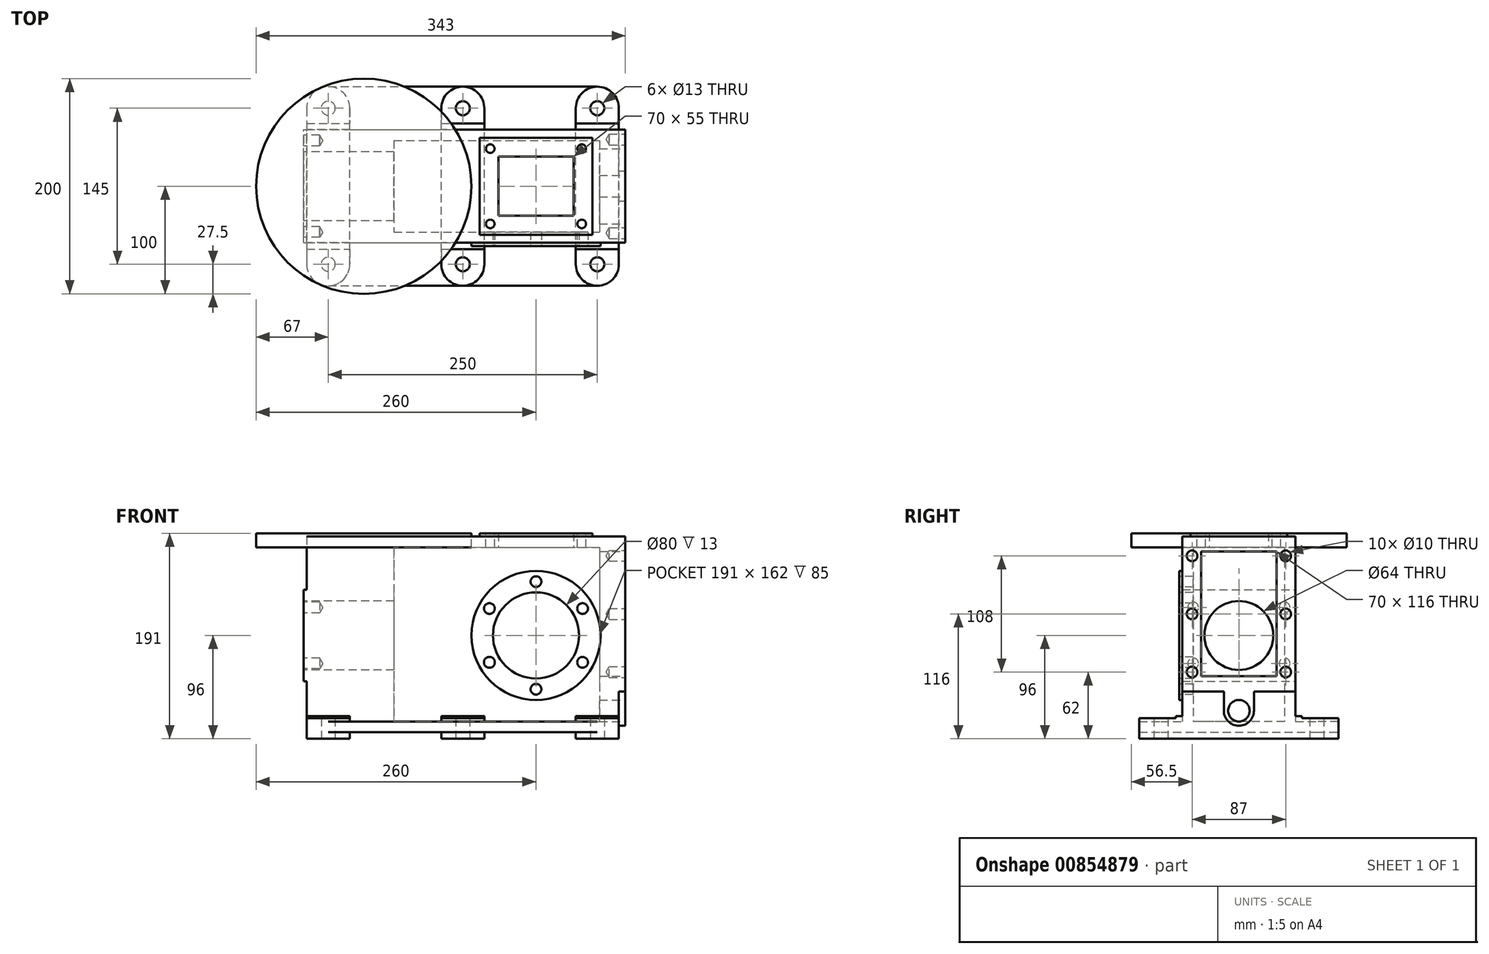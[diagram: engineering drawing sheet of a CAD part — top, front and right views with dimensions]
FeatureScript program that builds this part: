
annotation { "Feature Type Name" : "Feature", "Feature Type Description" : "" }
export const myFeature = defineFeature(function(context is Context, id is Id, definition is map)
    precondition{}
    {
        {
            var Q0;
            Q0=qCreatedBy(makeId("Top.planeOp"),FACE);
            cPlane(context, id + "F0", {"entities" : qUnion([Q0]), "cplaneType" : CPlaneType.OFFSET, "offset" : 90 * mm, "oppositeDirection" : true, "width" : 152.4 * mm, "height" : 152.4 * mm});
        }
        {
            var Q0;
            Q0=qCreatedBy(id+"F0.planeOp",FACE);
            var sketch = newSketch(context, id + "F1", { "sketchPlane" : qUnion([Q0])});
            skLineSegment(sketch, "E0", {"start": v(0, 0) * mm, "end": v(-193, 0) * mm, "construction": true});
            skLineSegment(sketch, "E1", {"start": v(-193, 72.5) * mm, "end": v(-193, -72.5) * mm, "construction": true});
            skLineSegment(sketch, "E2", {"start": v(-68, 72.5) * mm, "end": v(-68, -72.5) * mm, "construction": true});
            skLineSegment(sketch, "E3", {"start": v(57, 72.5) * mm, "end": v(57, -72.5) * mm, "construction": true});
            skLineSegment(sketch, "E4", {"start": v(-193, 72.5) * mm, "end": v(57, 72.5) * mm, "construction": true});
            skLineSegment(sketch, "E5", {"start": v(-193, -72.5) * mm, "end": v(57, -72.5) * mm, "construction": true});
            skArc(sketch, "E6", {"start": v(77, 72.5) * mm, "mid": v(57, 92.5) * mm, "end": v(37, 72.5) * mm});
            skArc(sketch, "E7", {"start": v(37, -72.5) * mm, "mid": v(57, -92.5) * mm, "end": v(77, -72.5) * mm});
            skLineSegment(sketch, "E8", {"start": v(37, 72.5) * mm, "end": v(37, -72.5) * mm});
            skLineSegment(sketch, "E9.MirrorCS", {"start": v(77, 72.5) * mm, "end": v(77, -72.5) * mm});
            skArc(sketch, "E10.1.0.0", {"start": v(-48, 72.5) * mm, "mid": v(-68, 92.5) * mm, "end": v(-88, 72.5) * mm});
            skLineSegment(sketch, "E10.1.0.1", {"start": v(-88, 72.5) * mm, "end": v(-88, -72.5) * mm});
            skLineSegment(sketch, "E10.1.0.2", {"start": v(-48, 72.5) * mm, "end": v(-48, -72.5) * mm});
            skArc(sketch, "E10.1.0.3", {"start": v(-88, -72.5) * mm, "mid": v(-68, -92.5) * mm, "end": v(-48, -72.5) * mm});
            skArc(sketch, "E10.2.0.0", {"start": v(-173, 72.5) * mm, "mid": v(-193, 92.5) * mm, "end": v(-213, 72.5) * mm});
            skLineSegment(sketch, "E10.2.0.1", {"start": v(-213, 72.5) * mm, "end": v(-213, -72.5) * mm});
            skLineSegment(sketch, "E10.2.0.2", {"start": v(-173, 72.5) * mm, "end": v(-173, -72.5) * mm});
            skArc(sketch, "E10.2.0.3", {"start": v(-213, -72.5) * mm, "mid": v(-193, -92.5) * mm, "end": v(-173, -72.5) * mm});
            skLineSegment(sketch, "E10.direction1", {"start": v(37, 72.5) * mm, "end": v(-88, 72.5) * mm, "construction": true});
            skCircle(sketch, "E11", {"center": v(57, 72.5) * mm, "radius": 6.5 * mm});
            skCircle(sketch, "E12", {"center": v(57, -72.5) * mm, "radius": 6.5 * mm});
            skCircle(sketch, "E13.1.0.0", {"center": v(-68, 72.5) * mm, "radius": 6.5 * mm});
            skCircle(sketch, "E13.1.0.1", {"center": v(-68, -72.5) * mm, "radius": 6.5 * mm});
            skCircle(sketch, "E13.2.0.0", {"center": v(-193, 72.5) * mm, "radius": 6.5 * mm});
            skCircle(sketch, "E13.2.0.1", {"center": v(-193, -72.5) * mm, "radius": 6.5 * mm});
            skLineSegment(sketch, "E13.direction1", {"start": v(57, 72.5) * mm, "end": v(-68, 72.5) * mm, "construction": true});
            skLineSegment(sketch, "E14", {"start": v(-193, 92.5) * mm, "end": v(57, 92.5) * mm});
            skLineSegment(sketch, "E15", {"start": v(-193, -92.5) * mm, "end": v(57, -92.5) * mm});
            skSolve(sketch);
        }
        {
            var Q0;
            Q0 = qSketchRegion(id + "F1", true);
            extrude(context, id + "F2", {"entities" : qUnion([Q0]), "depth" : 10 * mm, "offsetDistance" : 25 * mm});
        }
        {
            var Q0;
            Q0=makeQuery(id+"F2.opExtrude","CAP_FACE",FACE,{"disambiguationData":[OSD([sQuery(id+"F1.wireOp",EDGE,"E6"),sQuery(id+"F1.wireOp",EDGE,"E7"),sQuery(id+"F1.wireOp",EDGE,"E9.MirrorCS"),sQuery(id+"F1.wireOp",EDGE,"E10.2.0.0"),sQuery(id+"F1.wireOp",EDGE,"E10.2.0.1"),sQuery(id+"F1.wireOp",EDGE,"E10.2.0.3"),sQuery(id+"F1.wireOp",EDGE,"E11"),sQuery(id+"F1.wireOp",EDGE,"E12"),sQuery(id+"F1.wireOp",EDGE,"E13.1.0.0"),sQuery(id+"F1.wireOp",EDGE,"E13.1.0.1"),sQuery(id+"F1.wireOp",EDGE,"E13.2.0.0"),sQuery(id+"F1.wireOp",EDGE,"E13.2.0.1"),sQuery(id+"F1.wireOp",EDGE,"E14"),sQuery(id+"F1.wireOp",EDGE,"E15")])],"isStart":true});
            var sketch = newSketch(context, id + "F3", { "sketchPlane" : qUnion([Q0])});
            skLineSegment(sketch, "E16", {"start": v(0, 0) * mm, "end": v(-193, 0) * mm, "construction": true});
            skLineSegment(sketch, "E17", {"start": v(-193, 72.5) * mm, "end": v(-193, -72.5) * mm, "construction": true});
            skLineSegment(sketch, "E18", {"start": v(-68, 72.5) * mm, "end": v(-68, -72.5) * mm, "construction": true});
            skLineSegment(sketch, "E19", {"start": v(57, 72.5) * mm, "end": v(57, -72.5) * mm, "construction": true});
            skLineSegment(sketch, "E20", {"start": v(-193, 72.5) * mm, "end": v(57, 72.5) * mm, "construction": true});
            skLineSegment(sketch, "E21", {"start": v(-193, -72.5) * mm, "end": v(57, -72.5) * mm, "construction": true});
            skArc(sketch, "E22", {"start": v(77, 72.5) * mm, "mid": v(57, 92.5) * mm, "end": v(37, 72.5) * mm});
            skArc(sketch, "E23", {"start": v(37, -72.5) * mm, "mid": v(57, -92.5) * mm, "end": v(77, -72.5) * mm});
            skLineSegment(sketch, "E24", {"start": v(37, 72.5) * mm, "end": v(37, -72.5) * mm});
            skLineSegment(sketch, "E25.MirrorCS", {"start": v(77, 72.5) * mm, "end": v(77, -72.5) * mm});
            skArc(sketch, "E26.1.0.0", {"start": v(-48, 72.5) * mm, "mid": v(-68, 92.5) * mm, "end": v(-88, 72.5) * mm});
            skLineSegment(sketch, "E26.1.0.1", {"start": v(-88, 72.5) * mm, "end": v(-88, -72.5) * mm});
            skLineSegment(sketch, "E26.1.0.2", {"start": v(-48, 72.5) * mm, "end": v(-48, -72.5) * mm});
            skArc(sketch, "E26.1.0.3", {"start": v(-88, -72.5) * mm, "mid": v(-68, -92.5) * mm, "end": v(-48, -72.5) * mm});
            skArc(sketch, "E26.2.0.0", {"start": v(-173, 72.5) * mm, "mid": v(-193, 92.5) * mm, "end": v(-213, 72.5) * mm});
            skLineSegment(sketch, "E26.2.0.1", {"start": v(-213, 72.5) * mm, "end": v(-213, -72.5) * mm});
            skLineSegment(sketch, "E26.2.0.2", {"start": v(-173, 72.5) * mm, "end": v(-173, -72.5) * mm});
            skArc(sketch, "E26.2.0.3", {"start": v(-213, -72.5) * mm, "mid": v(-193, -92.5) * mm, "end": v(-173, -72.5) * mm});
            skLineSegment(sketch, "E26.direction1", {"start": v(37, 72.5) * mm, "end": v(-88, 72.5) * mm, "construction": true});
            skCircle(sketch, "E27", {"center": v(57, 72.5) * mm, "radius": 6.5 * mm});
            skCircle(sketch, "E28", {"center": v(57, -72.5) * mm, "radius": 6.5 * mm});
            skCircle(sketch, "E29.1.0.0", {"center": v(-68, 72.5) * mm, "radius": 6.5 * mm});
            skCircle(sketch, "E29.1.0.1", {"center": v(-68, -72.5) * mm, "radius": 6.5 * mm});
            skCircle(sketch, "E29.2.0.0", {"center": v(-193, 72.5) * mm, "radius": 6.5 * mm});
            skCircle(sketch, "E29.2.0.1", {"center": v(-193, -72.5) * mm, "radius": 6.5 * mm});
            skLineSegment(sketch, "E29.direction1", {"start": v(57, 72.5) * mm, "end": v(-68, 72.5) * mm, "construction": true});
            skSolve(sketch);
        }
        {
            var Q0;
            Q0 = qSketchRegion(id + "F3", true);
            extrude(context, id + "F4", {"entities" : qUnion([Q0]), "operationType" : NewBodyOperationType.ADD, "depth" : 6 * mm, "offsetDistance" : 25 * mm, "hasSecondDirection" : true, "secondDirectionOppositeDirection" : true, "secondDirectionDepth" : 15 * mm});
        }
        {
            var Q0;
            Q0=makeQuery(id+"F4.opExtrude","CAP_FACE",FACE,{"disambiguationData":[OSD([sQuery(id+"F3.wireOp",EDGE,"E26.2.0.0"),sQuery(id+"F3.wireOp",EDGE,"E26.2.0.1"),sQuery(id+"F3.wireOp",EDGE,"E26.2.0.2"),sQuery(id+"F3.wireOp",EDGE,"E26.2.0.3"),sQuery(id+"F3.wireOp",EDGE,"E29.2.0.0"),sQuery(id+"F3.wireOp",EDGE,"E29.2.0.1")])],"isStart":true});
            var sketch = newSketch(context, id + "F5", { "sketchPlane" : qUnion([Q0])});
            skLineSegment(sketch, "E30.bottom", {"start": v(-280.3, 116.13) * mm, "end": v(115.7, 116.13) * mm});
            skLineSegment(sketch, "E30.top", {"start": v(-280.3, 58.5) * mm, "end": v(115.7, 58.5) * mm});
            skLineSegment(sketch, "E30.left", {"start": v(-280.3, 116.13) * mm, "end": v(-280.3, 58.5) * mm});
            skLineSegment(sketch, "E30.right", {"start": v(115.7, 116.13) * mm, "end": v(115.7, 58.5) * mm});
            skLineSegment(sketch, "E31.bottom", {"start": v(-300.58, -58.5) * mm, "end": v(110.44, -58.5) * mm});
            skLineSegment(sketch, "E31.top", {"start": v(-300.58, -139.28) * mm, "end": v(110.44, -139.28) * mm});
            skLineSegment(sketch, "E31.left", {"start": v(-300.58, -58.5) * mm, "end": v(-300.58, -139.28) * mm});
            skLineSegment(sketch, "E31.right", {"start": v(110.44, -58.5) * mm, "end": v(110.44, -139.28) * mm});
            skSolve(sketch);
        }
        {
            var Q0;
            Q0 = qSketchRegion(id + "F5", true);
            extrude(context, id + "F6", {"entities" : qUnion([Q0]), "operationType" : NewBodyOperationType.REMOVE, "oppositeDirection" : true, "depth" : 2 * mm, "offsetDistance" : 25 * mm});
        }
        {
            var Q0;
            Q0=qCreatedBy(makeId("Front.planeOp"),FACE);
            var sketch = newSketch(context, id + "F7", { "sketchPlane" : qUnion([Q0])});
            skLineSegment(sketch, "E32.bottom", {"start": v(-213, 92) * mm, "end": v(77, 92) * mm});
            skLineSegment(sketch, "E32.top", {"start": v(-213, -80) * mm, "end": v(77, -80) * mm});
            skLineSegment(sketch, "E32.left", {"start": v(-213, 92) * mm, "end": v(-213, -80) * mm});
            skLineSegment(sketch, "E32.right", {"start": v(77, 92) * mm, "end": v(77, -80) * mm});
            skSolve(sketch);
        }
        {
            var Q0;
            Q0 = qSketchRegion(id + "F7", true);
            extrude(context, id + "F8", {"entities" : qUnion([Q0]), "operationType" : NewBodyOperationType.ADD, "depth" : 52.5 * mm, "offsetDistance" : 25 * mm, "hasSecondDirection" : true, "secondDirectionOppositeDirection" : true, "secondDirectionDepth" : 52.5 * mm});
        }
        {
            var Q0;
            Q0=qCreatedBy(makeId("Front.planeOp"),FACE);
            var sketch = newSketch(context, id + "F9", { "sketchPlane" : qUnion([Q0])});
            skLineSegment(sketch, "E33.bottom", {"start": v(-132, 82) * mm, "end": v(59, 82) * mm});
            skLineSegment(sketch, "E33.top", {"start": v(-132, -80) * mm, "end": v(59, -80) * mm});
            skLineSegment(sketch, "E33.left", {"start": v(-132, 82) * mm, "end": v(-132, -80) * mm});
            skLineSegment(sketch, "E33.right", {"start": v(59, 82) * mm, "end": v(59, -80) * mm});
            skLineSegment(sketch, "E34.0", {"start": v(-68, -80) * mm, "end": v(57, -80) * mm, "construction": true});
            skSolve(sketch);
        }
        {
            var Q0;
            Q0 = qSketchRegion(id + "F9", true);
            extrude(context, id + "F10", {"entities" : qUnion([Q0]), "operationType" : NewBodyOperationType.REMOVE, "oppositeDirection" : true, "depth" : (85 / 2) * mm, "offsetDistance" : 25 * mm, "hasSecondDirection" : true, "secondDirectionOppositeDirection" : false, "secondDirectionDepth" : (85 / 2) * mm});
        }
        {
            var Q0;
            Q0=makeQuery(id+"F8.boolean.opBoolean","MERGE",FACE,{"derivedFrom":[makeQuery(id+"F4.boolean.opBoolean","MERGE",FACE,{"derivedFrom":[makeQuery(id+"F2.opExtrude","SWEPT_FACE",FACE,{"disambiguationData":[OSD([sQuery(id+"F1.wireOp",EDGE,"E9.MirrorCS")])]}),makeQuery(id+"F4.opExtrude","SWEPT_FACE",FACE,{"disambiguationData":[OSD([sQuery(id+"F3.wireOp",EDGE,"E25.MirrorCS")])]})]}),makeQuery(id+"F8.opExtrude","SWEPT_FACE",FACE,{"disambiguationData":[OSD([sQuery(id+"F7.wireOp",EDGE,"E32.right")])]})]});
            var sketch = newSketch(context, id + "F11", { "sketchPlane" : qUnion([Q0])});
            skLineSegment(sketch, "E35.0", {"start": v(-52.5, 92) * mm, "end": v(52.5, 92) * mm});
            skLineSegment(sketch, "E35.1", {"start": v(-52.5, 92) * mm, "end": v(-52.5, -75) * mm});
            skLineSegment(sketch, "E35.2", {"start": v(52.5, 92) * mm, "end": v(52.5, -75) * mm});
            skLineSegment(sketch, "E36", {"start": v(-52.5, -52) * mm, "end": v(-14, -52) * mm});
            skLineSegment(sketch, "E37", {"start": v(0, 92) * mm, "end": v(0, -70) * mm, "construction": true});
            skArc(sketch, "E38", {"start": v(-14, -70) * mm, "mid": v(0, -84) * mm, "end": v(14, -70) * mm});
            skLineSegment(sketch, "E39", {"start": v(-14, -70) * mm, "end": v(14, -70) * mm, "construction": true});
            skLineSegment(sketch, "E40", {"start": v(-14, -70) * mm, "end": v(-14, -52) * mm});
            skLineSegment(sketch, "E41", {"start": v(14, -70) * mm, "end": v(14, -52) * mm});
            skLineSegment(sketch, "E42.trimOffspring", {"start": v(14, -52) * mm, "end": v(52.5, -52) * mm});
            skSolve(sketch);
        }
        {
            var Q0;
            Q0 = qSketchRegion(id + "F11", true);
            extrude(context, id + "F12", {"entities" : qUnion([Q0]), "operationType" : NewBodyOperationType.ADD, "depth" : 6 * mm, "offsetDistance" : 25 * mm});
        }
        {
            var Q0;
            Q0=makeQuery(id+"F12.opExtrude","CAP_FACE",FACE,{"disambiguationData":[OSD([sQuery(id+"F11.wireOp",EDGE,"E35.0"),sQuery(id+"F11.wireOp",EDGE,"E35.1"),sQuery(id+"F11.wireOp",EDGE,"E35.2"),sQuery(id+"F11.wireOp",EDGE,"E36"),sQuery(id+"F11.wireOp",EDGE,"E38"),sQuery(id+"F11.wireOp",EDGE,"E40"),sQuery(id+"F11.wireOp",EDGE,"E41"),sQuery(id+"F11.wireOp",EDGE,"E42.trimOffspring")])],"isStart":false});
            var sketch = newSketch(context, id + "F13", { "sketchPlane" : qUnion([Q0])});
            skLineSegment(sketch, "E43.bottom", {"start": v(-35, 78) * mm, "end": v(35, 78) * mm});
            skLineSegment(sketch, "E43.top", {"start": v(-35, -38) * mm, "end": v(35, -38) * mm});
            skLineSegment(sketch, "E43.left", {"start": v(-35, 78) * mm, "end": v(-35, -38) * mm});
            skLineSegment(sketch, "E43.right", {"start": v(35, 78) * mm, "end": v(35, -38) * mm});
            skLineSegment(sketch, "E44", {"start": v(-35, 20) * mm, "end": v(35, 20) * mm, "construction": true});
            skSolve(sketch);
        }
        {
            var Q0;
            Q0 = qSketchRegion(id + "F13", true);
            extrude(context, id + "F14", {"entities" : qUnion([Q0]), "operationType" : NewBodyOperationType.REMOVE, "endBound" : BoundingType.UP_TO_NEXT, "oppositeDirection" : true, "depth" : 25 * mm, "offsetDistance" : 25 * mm});
        }
        {
            var Q0;
            Q0=makeQuery(id+"F12.opExtrude","CAP_FACE",FACE,{"disambiguationData":[OSD([sQuery(id+"F11.wireOp",EDGE,"E35.0"),sQuery(id+"F11.wireOp",EDGE,"E35.1"),sQuery(id+"F11.wireOp",EDGE,"E35.2"),sQuery(id+"F11.wireOp",EDGE,"E36"),sQuery(id+"F11.wireOp",EDGE,"E38"),sQuery(id+"F11.wireOp",EDGE,"E40"),sQuery(id+"F11.wireOp",EDGE,"E41"),sQuery(id+"F11.wireOp",EDGE,"E42.trimOffspring")])],"isStart":false});
            var sketch = newSketch(context, id + "F15", { "sketchPlane" : qUnion([Q0])});
            skCircle(sketch, "E45", {"center": v(0, -70) * mm, "radius": 9 * mm});
            skSolve(sketch);
        }
        {
            var Q0;
            Q0=sQuery(id+"F15.wireOp",VERTEX,"E45.center");
            var Q1;
            Q1=makeQuery(id+"F2.opExtrude","SWEPT_BODY",BODY,{"disambiguationData":[OSD([sQuery(id+"F1.wireOp",EDGE,"E6"),sQuery(id+"F1.wireOp",EDGE,"E7"),sQuery(id+"F1.wireOp",EDGE,"E9.MirrorCS"),sQuery(id+"F1.wireOp",EDGE,"E10.2.0.0"),sQuery(id+"F1.wireOp",EDGE,"E10.2.0.1"),sQuery(id+"F1.wireOp",EDGE,"E10.2.0.3"),sQuery(id+"F1.wireOp",EDGE,"E11"),sQuery(id+"F1.wireOp",EDGE,"E12"),sQuery(id+"F1.wireOp",EDGE,"E13.1.0.0"),sQuery(id+"F1.wireOp",EDGE,"E13.1.0.1"),sQuery(id+"F1.wireOp",EDGE,"E13.2.0.0"),sQuery(id+"F1.wireOp",EDGE,"E13.2.0.1"),sQuery(id+"F1.wireOp",EDGE,"E14"),sQuery(id+"F1.wireOp",EDGE,"E15")])]});
            hole(context, id + "F16", {"style" : HoleStyle.SIMPLE, "endStyle" : HoleEndStyle.BLIND, "holeDiameter" : 20 * mm, "majorDiameter" : 5 * mm, "holeDepth" : 40 * mm, "isTappedThrough" : true, "tappedDepth" : 12 * mm, "tapClearance" : 3, "locations" : qUnion([Q0]), "scope" : qUnion([Q1])});
        }
        {
            var Q0;
            Q0=makeQuery(id+"F12.opExtrude","CAP_FACE",FACE,{"disambiguationData":[OSD([sQuery(id+"F11.wireOp",EDGE,"E35.0"),sQuery(id+"F11.wireOp",EDGE,"E35.1"),sQuery(id+"F11.wireOp",EDGE,"E35.2"),sQuery(id+"F11.wireOp",EDGE,"E36"),sQuery(id+"F11.wireOp",EDGE,"E38"),sQuery(id+"F11.wireOp",EDGE,"E40"),sQuery(id+"F11.wireOp",EDGE,"E41"),sQuery(id+"F11.wireOp",EDGE,"E42.trimOffspring")])],"isStart":false});
            var sketch = newSketch(context, id + "F17", { "sketchPlane" : qUnion([Q0])});
            skLineSegment(sketch, "E46", {"start": v(-43.5, 74) * mm, "end": v(-43.5, -34) * mm, "construction": true});
            skLineSegment(sketch, "E47", {"start": v(43.5, 74) * mm, "end": v(43.5, -34) * mm, "construction": true});
            skLineSegment(sketch, "E48", {"start": v(-43.5, 74) * mm, "end": v(43.5, 74) * mm, "construction": true});
            skLineSegment(sketch, "E49", {"start": v(-43.5, -34) * mm, "end": v(43.5, -34) * mm, "construction": true});
            skLineSegment(sketch, "E50", {"start": v(-43.5, 20) * mm, "end": v(43.5, 20) * mm, "construction": true});
            skCircle(sketch, "E51", {"center": v(-43.5, 74) * mm, "radius": 5 * mm});
            skCircle(sketch, "E52.MirrorC", {"center": v(43.5, 74) * mm, "radius": 5 * mm});
            skCircle(sketch, "E53.MirrorC", {"center": v(-43.5, -34) * mm, "radius": 5 * mm});
            skCircle(sketch, "E54.MirrorC", {"center": v(43.5, -34) * mm, "radius": 5 * mm});
            skCircle(sketch, "E55", {"center": v(-43.5, 20) * mm, "radius": 5 * mm});
            skCircle(sketch, "E56", {"center": v(43.5, 20) * mm, "radius": 5 * mm});
            skSolve(sketch);
        }
        {
            var Q0;
            Q0=sQuery(id+"F17.wireOp",VERTEX,"E46.start");
            var Q1;
            Q1=sQuery(id+"F17.wireOp",VERTEX,"E50.start");
            var Q2;
            Q2=sQuery(id+"F17.wireOp",VERTEX,"E46.end");
            var Q3;
            Q3=sQuery(id+"F17.wireOp",VERTEX,"E47.start");
            var Q4;
            Q4=sQuery(id+"F17.wireOp",VERTEX,"E50.end");
            var Q5;
            Q5=sQuery(id+"F17.wireOp",VERTEX,"E47.end");
            var Q6;
            Q6=makeQuery(id+"F2.opExtrude","SWEPT_BODY",BODY,{"disambiguationData":[OSD([sQuery(id+"F1.wireOp",EDGE,"E6"),sQuery(id+"F1.wireOp",EDGE,"E7"),sQuery(id+"F1.wireOp",EDGE,"E9.MirrorCS"),sQuery(id+"F1.wireOp",EDGE,"E10.2.0.0"),sQuery(id+"F1.wireOp",EDGE,"E10.2.0.1"),sQuery(id+"F1.wireOp",EDGE,"E10.2.0.3"),sQuery(id+"F1.wireOp",EDGE,"E11"),sQuery(id+"F1.wireOp",EDGE,"E12"),sQuery(id+"F1.wireOp",EDGE,"E13.1.0.0"),sQuery(id+"F1.wireOp",EDGE,"E13.1.0.1"),sQuery(id+"F1.wireOp",EDGE,"E13.2.0.0"),sQuery(id+"F1.wireOp",EDGE,"E13.2.0.1"),sQuery(id+"F1.wireOp",EDGE,"E14"),sQuery(id+"F1.wireOp",EDGE,"E15")])]});
            hole(context, id + "F18", {"style" : HoleStyle.SIMPLE, "endStyle" : HoleEndStyle.BLIND, "holeDiameter" : 10 * mm, "majorDiameter" : 5 * mm, "holeDepth" : 15 * mm, "isTappedThrough" : true, "tappedDepth" : 12 * mm, "tapClearance" : 3, "locations" : qUnion([Q0, Q1, Q2, Q3, Q4, Q5]), "scope" : qUnion([Q6])});
        }
        {
            var Q0;
            Q0=makeQuery(id+"F12.boolean.opBoolean","MERGE",FACE,{"derivedFrom":[makeQuery(id+"F8.opExtrude","SWEPT_FACE",FACE,{"disambiguationData":[OSD([sQuery(id+"F7.wireOp",EDGE,"E32.bottom")])]}),makeQuery(id+"F12.opExtrude","SWEPT_FACE",FACE,{"disambiguationData":[OSD([sQuery(id+"F11.wireOp",EDGE,"E35.0")])]})]});
            var sketch = newSketch(context, id + "F19", { "sketchPlane" : qUnion([Q0])});
            skLineSegment(sketch, "E57.bottom", {"start": v(-52.5, 45) * mm, "end": v(52.5, 45) * mm});
            skLineSegment(sketch, "E57.top", {"start": v(-52.5, -45) * mm, "end": v(52.5, -45) * mm});
            skLineSegment(sketch, "E57.left", {"start": v(-52.5, 45) * mm, "end": v(-52.5, -45) * mm});
            skLineSegment(sketch, "E57.right", {"start": v(52.5, 45) * mm, "end": v(52.5, -45) * mm});
            skPoint(sketch, "E57.middle", {"position": v(0, 0) * mm});
            skLineSegment(sketch, "E58.bottom", {"start": v(-35, 27.5) * mm, "end": v(35, 27.5) * mm});
            skLineSegment(sketch, "E58.top", {"start": v(-35, -27.5) * mm, "end": v(35, -27.5) * mm});
            skLineSegment(sketch, "E58.left", {"start": v(-35, 27.5) * mm, "end": v(-35, -27.5) * mm});
            skLineSegment(sketch, "E58.right", {"start": v(35, 27.5) * mm, "end": v(35, -27.5) * mm});
            skSolve(sketch);
        }
        {
            var Q0;
            Q0 = qSketchRegion(id + "F19", true);
            extrude(context, id + "F20", {"entities" : qUnion([Q0]), "operationType" : NewBodyOperationType.ADD, "depth" : 3 * mm, "offsetDistance" : 25 * mm});
        }
        {
            var Q0;
            Q0=makeQuery(id+"F20.boolean.opBoolean","SPLIT",FACE,{"disambiguationData":[TD([makeQuery(id+"F20.opExtrude","SWEPT_FACE",FACE,{"disambiguationData":[OSD([sQuery(id+"F19.wireOp",EDGE,"E58.bottom")])]})])],"derivedFrom":makeQuery(id+"F12.boolean.opBoolean","MERGE",FACE,{"derivedFrom":[makeQuery(id+"F8.opExtrude","SWEPT_FACE",FACE,{"disambiguationData":[OSD([sQuery(id+"F7.wireOp",EDGE,"E32.bottom")])]}),makeQuery(id+"F12.opExtrude","SWEPT_FACE",FACE,{"disambiguationData":[OSD([sQuery(id+"F11.wireOp",EDGE,"E35.0")])]})]})});
            extrude(context, id + "F21", {"entities" : qUnion([Q0]), "operationType" : NewBodyOperationType.REMOVE, "endBound" : BoundingType.UP_TO_NEXT, "oppositeDirection" : true, "depth" : 25 * mm, "offsetDistance" : 25 * mm});
        }
        {
            var Q0;
            Q0=makeQuery(id+"F20.opExtrude","CAP_FACE",FACE,{"disambiguationData":[OSD([sQuery(id+"F19.wireOp",EDGE,"E57.bottom"),sQuery(id+"F19.wireOp",EDGE,"E57.top"),sQuery(id+"F19.wireOp",EDGE,"E57.left"),sQuery(id+"F19.wireOp",EDGE,"E57.right"),sQuery(id+"F19.wireOp",EDGE,"E58.bottom"),sQuery(id+"F19.wireOp",EDGE,"E58.top"),sQuery(id+"F19.wireOp",EDGE,"E58.left"),sQuery(id+"F19.wireOp",EDGE,"E58.right")])],"isStart":false});
            var sketch = newSketch(context, id + "F22", { "sketchPlane" : qUnion([Q0])});
            skLineSegment(sketch, "E59", {"start": v(-42.5, 35) * mm, "end": v(42.5, 35) * mm, "construction": true});
            skLineSegment(sketch, "E60", {"start": v(-42.5, -35) * mm, "end": v(42.5, -35) * mm, "construction": true});
            skLineSegment(sketch, "E61", {"start": v(-42.5, 35) * mm, "end": v(-42.5, -35) * mm, "construction": true});
            skLineSegment(sketch, "E62", {"start": v(42.5, 35) * mm, "end": v(42.5, -35) * mm, "construction": true});
            skCircle(sketch, "E63", {"center": v(-42.5, 35) * mm, "radius": 4 * mm});
            skCircle(sketch, "E64.MirrorC", {"center": v(42.5, 35) * mm, "radius": 4 * mm});
            skCircle(sketch, "E65.MirrorC", {"center": v(42.5, -35) * mm, "radius": 4 * mm});
            skCircle(sketch, "E66.MirrorC", {"center": v(-42.5, -35) * mm, "radius": 4 * mm});
            skSolve(sketch);
        }
        {
            var Q0;
            Q0 = qSketchRegion(id + "F22", true);
            extrude(context, id + "F23", {"entities" : qUnion([Q0]), "operationType" : NewBodyOperationType.REMOVE, "oppositeDirection" : true, "depth" : 25 * mm, "offsetDistance" : 25 * mm});
        }
        {
            var Q0;
            Q0=makeQuery(id+"F8.boolean.opBoolean","MERGE",FACE,{"derivedFrom":[makeQuery(id+"F4.boolean.opBoolean","MERGE",FACE,{"derivedFrom":[makeQuery(id+"F2.opExtrude","SWEPT_FACE",FACE,{"disambiguationData":[OSD([sQuery(id+"F1.wireOp",EDGE,"E10.2.0.1")])]}),makeQuery(id+"F4.opExtrude","SWEPT_FACE",FACE,{"disambiguationData":[OSD([sQuery(id+"F3.wireOp",EDGE,"E26.2.0.1")])]})]}),makeQuery(id+"F8.opExtrude","SWEPT_FACE",FACE,{"disambiguationData":[OSD([sQuery(id+"F7.wireOp",EDGE,"E32.left")])]})]});
            var sketch = newSketch(context, id + "F24", { "sketchPlane" : qUnion([Q0])});
            skLineSegment(sketch, "E67.bottom", {"start": v(52.5, 42.5) * mm, "end": v(-52.5, 42.5) * mm});
            skLineSegment(sketch, "E67.top", {"start": v(52.5, -42.5) * mm, "end": v(-52.5, -42.5) * mm});
            skLineSegment(sketch, "E67.left", {"start": v(52.5, 42.5) * mm, "end": v(52.5, -42.5) * mm});
            skLineSegment(sketch, "E67.right", {"start": v(-52.5, 42.5) * mm, "end": v(-52.5, -42.5) * mm});
            skPoint(sketch, "E67.middle", {"position": v(0, 0) * mm});
            skSolve(sketch);
        }
        {
            var Q0;
            Q0 = qSketchRegion(id + "F24", true);
            extrude(context, id + "F25", {"entities" : qUnion([Q0]), "operationType" : NewBodyOperationType.ADD, "depth" : 3 * mm, "offsetDistance" : 25 * mm});
        }
        {
            var Q0;
            Q0=makeQuery(id+"F25.opExtrude","CAP_FACE",FACE,{"disambiguationData":[OSD([sQuery(id+"F24.wireOp",EDGE,"E67.bottom"),sQuery(id+"F24.wireOp",EDGE,"E67.top"),sQuery(id+"F24.wireOp",EDGE,"E67.left"),sQuery(id+"F24.wireOp",EDGE,"E67.right")])],"isStart":false});
            var sketch = newSketch(context, id + "F26", { "sketchPlane" : qUnion([Q0])});
            skCircle(sketch, "E68", {"center": v(0, 0) * mm, "radius": 32 * mm});
            skSolve(sketch);
        }
        {
            var Q0;
            Q0 = qSketchRegion(id + "F26", true);
            extrude(context, id + "F27", {"entities" : qUnion([Q0]), "operationType" : NewBodyOperationType.REMOVE, "endBound" : BoundingType.UP_TO_NEXT, "oppositeDirection" : true, "depth" : 25 * mm, "offsetDistance" : 25 * mm});
        }
        {
            var Q0;
            Q0=makeQuery(id+"F25.opExtrude","CAP_FACE",FACE,{"disambiguationData":[OSD([sQuery(id+"F24.wireOp",EDGE,"E67.bottom"),sQuery(id+"F24.wireOp",EDGE,"E67.top"),sQuery(id+"F24.wireOp",EDGE,"E67.left"),sQuery(id+"F24.wireOp",EDGE,"E67.right")])],"isStart":false});
            var sketch = newSketch(context, id + "F28", { "sketchPlane" : qUnion([Q0])});
            skLineSegment(sketch, "E69", {"start": v(-42.5, 26) * mm, "end": v(-42.5, -26) * mm, "construction": true});
            skLineSegment(sketch, "E70", {"start": v(42.5, 26) * mm, "end": v(42.5, -26) * mm, "construction": true});
            skLineSegment(sketch, "E71", {"start": v(-42.5, 26) * mm, "end": v(42.5, 26) * mm, "construction": true});
            skLineSegment(sketch, "E72", {"start": v(-42.5, -26) * mm, "end": v(42.5, -26) * mm, "construction": true});
            skCircle(sketch, "E73", {"center": v(-42.5, 26) * mm, "radius": 5 * mm});
            skCircle(sketch, "E74.MirrorC", {"center": v(42.5, 26) * mm, "radius": 5 * mm});
            skCircle(sketch, "E75.MirrorC", {"center": v(-42.5, -26) * mm, "radius": 5 * mm});
            skCircle(sketch, "E76.MirrorC", {"center": v(42.5, -26) * mm, "radius": 5 * mm});
            skSolve(sketch);
        }
        {
            var Q0;
            Q0=sQuery(id+"F28.wireOp",VERTEX,"E69.start");
            var Q1;
            Q1=sQuery(id+"F28.wireOp",VERTEX,"E70.end");
            var Q2;
            Q2=sQuery(id+"F28.wireOp",VERTEX,"E69.end");
            var Q3;
            Q3=sQuery(id+"F28.wireOp",VERTEX,"E70.start");
            var Q4;
            Q4=makeQuery(id+"F2.opExtrude","SWEPT_BODY",BODY,{"disambiguationData":[OSD([sQuery(id+"F1.wireOp",EDGE,"E6"),sQuery(id+"F1.wireOp",EDGE,"E7"),sQuery(id+"F1.wireOp",EDGE,"E9.MirrorCS"),sQuery(id+"F1.wireOp",EDGE,"E10.2.0.0"),sQuery(id+"F1.wireOp",EDGE,"E10.2.0.1"),sQuery(id+"F1.wireOp",EDGE,"E10.2.0.3"),sQuery(id+"F1.wireOp",EDGE,"E11"),sQuery(id+"F1.wireOp",EDGE,"E12"),sQuery(id+"F1.wireOp",EDGE,"E13.1.0.0"),sQuery(id+"F1.wireOp",EDGE,"E13.1.0.1"),sQuery(id+"F1.wireOp",EDGE,"E13.2.0.0"),sQuery(id+"F1.wireOp",EDGE,"E13.2.0.1"),sQuery(id+"F1.wireOp",EDGE,"E14"),sQuery(id+"F1.wireOp",EDGE,"E15")])]});
            hole(context, id + "F29", {"style" : HoleStyle.SIMPLE, "endStyle" : HoleEndStyle.BLIND, "holeDiameter" : 10 * mm, "majorDiameter" : 5 * mm, "holeDepth" : 15 * mm, "isTappedThrough" : true, "tappedDepth" : 12 * mm, "tapClearance" : 3, "locations" : qUnion([Q0, Q1, Q2, Q3]), "scope" : qUnion([Q4])});
        }
        {
            var Q0;
            Q0=makeQuery(id+"F25.boolean.opBoolean","MERGE",FACE,{"derivedFrom":[makeQuery(id+"F12.boolean.opBoolean","MERGE",FACE,{"derivedFrom":[makeQuery(id+"F8.opExtrude","CAP_FACE",FACE,{"disambiguationData":[OSD([sQuery(id+"F7.wireOp",EDGE,"E32.bottom"),sQuery(id+"F7.wireOp",EDGE,"E32.top"),sQuery(id+"F7.wireOp",EDGE,"E32.left"),sQuery(id+"F7.wireOp",EDGE,"E32.right")])],"isStart":false}),makeQuery(id+"F12.opExtrude","SWEPT_FACE",FACE,{"disambiguationData":[OSD([sQuery(id+"F11.wireOp",EDGE,"E35.1")])]})]}),makeQuery(id+"F25.opExtrude","SWEPT_FACE",FACE,{"disambiguationData":[OSD([sQuery(id+"F24.wireOp",EDGE,"E67.left")])]})]});
            var sketch = newSketch(context, id + "F30", { "sketchPlane" : qUnion([Q0])});
            skCircle(sketch, "E77", {"center": v(0, 0) * mm, "radius": 60 * mm});
            skSolve(sketch);
        }
        {
            var Q0;
            Q0 = qSketchRegion(id + "F30", true);
            extrude(context, id + "F31", {"entities" : qUnion([Q0]), "operationType" : NewBodyOperationType.ADD, "depth" : 3 * mm, "offsetDistance" : 25 * mm});
        }
        {
            var Q0;
            Q0=makeQuery(id+"F31.opExtrude","CAP_FACE",FACE,{"disambiguationData":[OSD([sQuery(id+"F30.wireOp",EDGE,"E77")])],"isStart":false});
            var sketch = newSketch(context, id + "F32", { "sketchPlane" : qUnion([Q0])});
            skCircle(sketch, "E78", {"center": v(0, 0) * mm, "radius": 40 * mm});
            skSolve(sketch);
        }
        {
            var Q0;
            Q0 = qSketchRegion(id + "F32", true);
            extrude(context, id + "F33", {"entities" : qUnion([Q0]), "operationType" : NewBodyOperationType.REMOVE, "endBound" : BoundingType.UP_TO_NEXT, "oppositeDirection" : true, "depth" : 25 * mm, "offsetDistance" : 25 * mm});
        }
        {
            var Q0;
            Q0=makeQuery(id+"F31.opExtrude","CAP_FACE",FACE,{"disambiguationData":[OSD([sQuery(id+"F30.wireOp",EDGE,"E77")])],"isStart":false});
            var sketch = newSketch(context, id + "F34", { "sketchPlane" : qUnion([Q0])});
            skCircle(sketch, "E79", {"center": v(0, 0) * mm, "radius": 50 * mm, "construction": true});
            skLineSegment(sketch, "E80", {"start": v(0, 0) * mm, "end": v(43.3, 25) * mm, "construction": true});
            skCircle(sketch, "E81", {"center": v(43.3, 25) * mm, "radius": 5 * mm});
            skCircle(sketch, "E82.1.0", {"center": v(-43.3, 25) * mm, "radius": 5 * mm});
            skCircle(sketch, "E82.2.0", {"center": v(0, -50) * mm, "radius": 5 * mm});
            skCircle(sketch, "E83.MirrorC", {"center": v(0, 50) * mm, "radius": 5 * mm});
            skCircle(sketch, "E84.MirrorC", {"center": v(43.3, -25) * mm, "radius": 5 * mm});
            skCircle(sketch, "E85.MirrorC", {"center": v(-43.3, -25) * mm, "radius": 5 * mm});
            skSolve(sketch);
        }
        {
            var Q0;
            Q0=sQuery(id+"F34.wireOp",VERTEX,"E83.MirrorC.center");
            var Q1;
            Q1=sQuery(id+"F34.wireOp",VERTEX,"E80.end");
            var Q2;
            Q2=sQuery(id+"F34.wireOp",VERTEX,"E84.MirrorC.center");
            var Q3;
            Q3=sQuery(id+"F34.wireOp",VERTEX,"E82.2.0.center");
            var Q4;
            Q4=sQuery(id+"F34.wireOp",VERTEX,"E85.MirrorC.center");
            var Q5;
            Q5=sQuery(id+"F34.wireOp",VERTEX,"E82.1.0.center");
            var Q6;
            Q6=makeQuery(id+"F2.opExtrude","SWEPT_BODY",BODY,{"disambiguationData":[OSD([sQuery(id+"F1.wireOp",EDGE,"E6"),sQuery(id+"F1.wireOp",EDGE,"E7"),sQuery(id+"F1.wireOp",EDGE,"E9.MirrorCS"),sQuery(id+"F1.wireOp",EDGE,"E10.2.0.0"),sQuery(id+"F1.wireOp",EDGE,"E10.2.0.1"),sQuery(id+"F1.wireOp",EDGE,"E10.2.0.3"),sQuery(id+"F1.wireOp",EDGE,"E11"),sQuery(id+"F1.wireOp",EDGE,"E12"),sQuery(id+"F1.wireOp",EDGE,"E13.1.0.0"),sQuery(id+"F1.wireOp",EDGE,"E13.1.0.1"),sQuery(id+"F1.wireOp",EDGE,"E13.2.0.0"),sQuery(id+"F1.wireOp",EDGE,"E13.2.0.1"),sQuery(id+"F1.wireOp",EDGE,"E14"),sQuery(id+"F1.wireOp",EDGE,"E15")])]});
            hole(context, id + "F35", {"style" : HoleStyle.SIMPLE, "endStyle" : HoleEndStyle.BLIND, "holeDiameter" : 10 * mm, "majorDiameter" : 5 * mm, "holeDepth" : 15 * mm, "isTappedThrough" : true, "tappedDepth" : 12 * mm, "tapClearance" : 3, "locations" : qUnion([Q0, Q1, Q2, Q3, Q4, Q5]), "scope" : qUnion([Q6])});
        }
        {
            var Q0;
            Q0=makeQuery(id+"F20.opExtrude","CAP_FACE",FACE,{"disambiguationData":[OSD([sQuery(id+"F19.wireOp",EDGE,"E57.bottom"),sQuery(id+"F19.wireOp",EDGE,"E57.top"),sQuery(id+"F19.wireOp",EDGE,"E57.left"),sQuery(id+"F19.wireOp",EDGE,"E57.right"),sQuery(id+"F19.wireOp",EDGE,"E58.bottom"),sQuery(id+"F19.wireOp",EDGE,"E58.top"),sQuery(id+"F19.wireOp",EDGE,"E58.left"),sQuery(id+"F19.wireOp",EDGE,"E58.right")])],"isStart":false});
            var sketch = newSketch(context, id + "F36", { "sketchPlane" : qUnion([Q0])});
            skLineSegment(sketch, "E86", {"start": v(-160, 0) * mm, "end": v(0, 0) * mm, "construction": true});
            skLineSegment(sketch, "E87", {"start": v(-160, 117.37) * mm, "end": v(-160, -129.13) * mm, "construction": true});
            skCircle(sketch, "E88", {"center": v(-160, 0) * mm, "radius": 100 * mm});
            skSolve(sketch);
        }
        {
            var Q0;
            Q0 = qSketchRegion(id + "F36", true);
            extrude(context, id + "F37", {"entities" : qUnion([Q0]), "oppositeDirection" : true, "depth" : 13 * mm, "offsetDistance" : 25 * mm});
        }
        {
            var Q0;
            Q0=qCreatedBy(makeId("Right.planeOp"),FACE);
            cPlane(context, id + "F38", {"entities" : qUnion([Q0]), "cplaneType" : CPlaneType.OFFSET, "offset" : 160 * mm, "oppositeDirection" : true, "width" : 150 * mm, "height" : 150 * mm});
        }
    });
